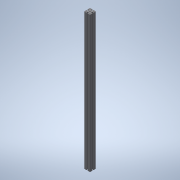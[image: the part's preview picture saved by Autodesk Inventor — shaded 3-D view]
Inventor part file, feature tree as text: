
AUTODESK INVENTOR PART (.ipt)
format: ipt  version: 2022 (Build 260153000, 153)  size: 224,768 bytes
history: native  units: mm (DEFAULTED — no unit token found)
features: other x21, sketch x2, extrude x1, hole x1
ambient origin geometry x8: Origin, YZ Plane, XZ Plane, XY Plane, X Axis, Y Axis, Z Axis, Center Point
bodies: Solid1 (feature_tree)
feature tree (25):
  extrude  "Extrusion1"  TaperAngle=0.0deg  [1 undecoded]
  hole  "Hole1"  [1 undecoded]
  other  "C1_XY"
  other  "C1_YZ"
  other  "C1_ZX"
  other  "C1_X"
  other  "C1_Y"
  other  "C1_Z"
  other  "C1_Center"
  other  "to_frame_cap1_XY"
  other  "to_frame_cap1_YZ"
  other  "to_frame_cap1_ZX"
  other  "to_frame_cap1_X"
  other  "to_frame_cap1_Y"
  other  "to_frame_cap1_Z"
  other  "to_frame_cap1_Center"
  other  "to_frame_cap2_XY"
  other  "to_frame_cap2_YZ"
  other  "to_frame_cap2_ZX"
  other  "to_frame_cap2_X"
  other  "to_frame_cap2_Y"
  other  "to_frame_cap2_Z"
  other  "to_frame_cap2_Center"
  sketch  "Sketch_60"  dims[d2=10.5mm d3=6.0mm d4=4.0mm d5=2.0mm d6=90.0deg d7=1000.0mm d8=0.0mm d9=0.0mm d10=0.0mm d11=0.0mm d12=152.4mm d13=0.872665mm d14=152.4mm d15=0.872665mm]
  sketch  "Sketch2"  dims[d0=1371.6mm d1=0.0mm]
note: 2 required parameter values undecoded (feature->parameter linkage not recoverable at this tier; creation-order binding heuristic only, values carry confidence <= 0.55)
